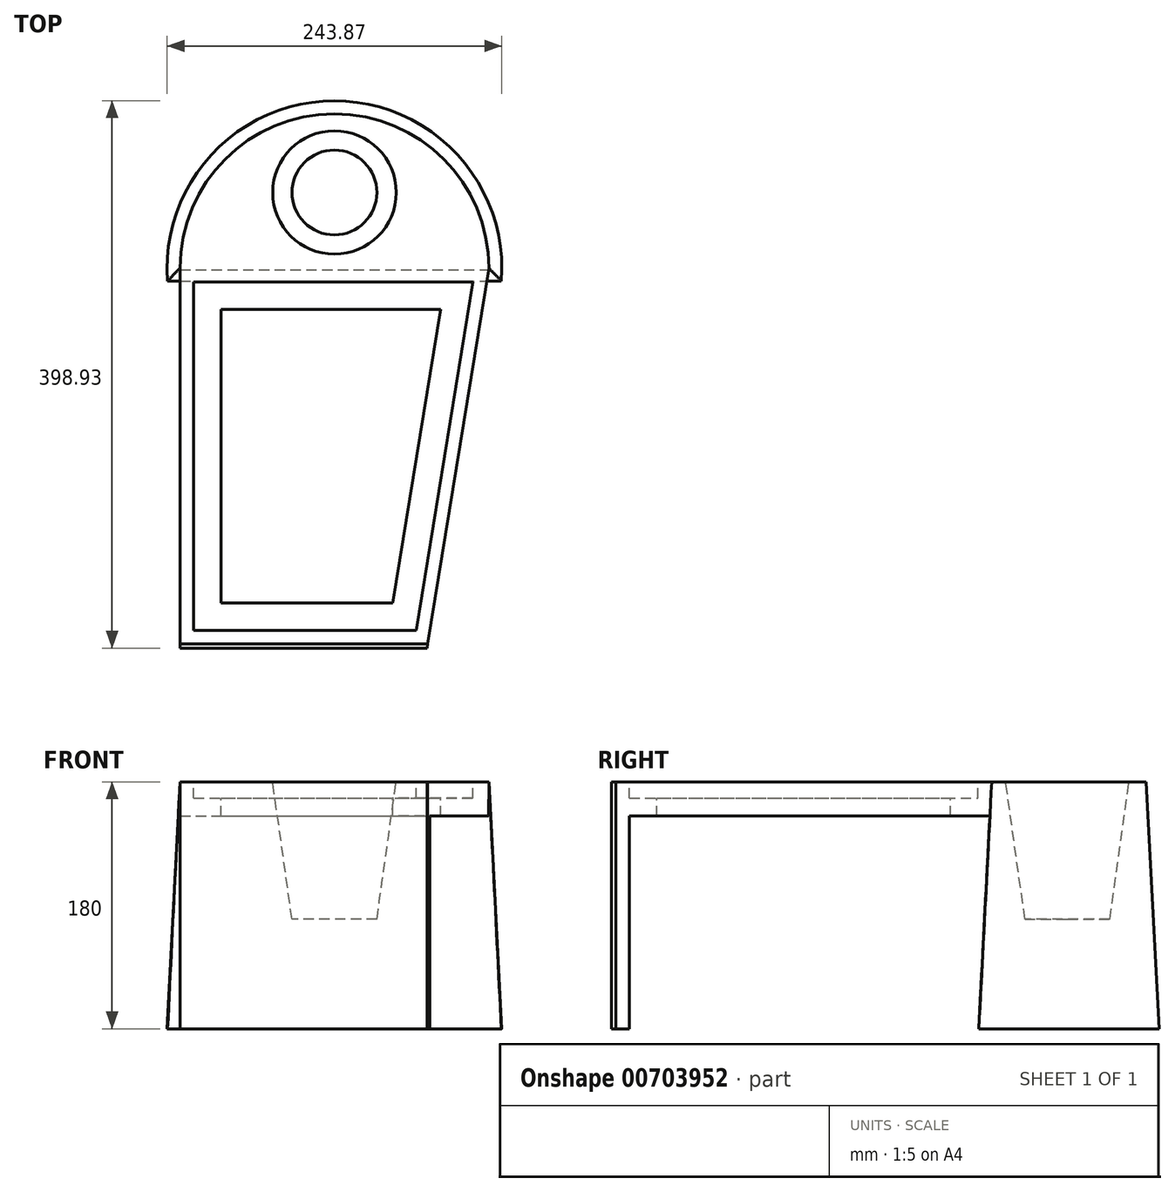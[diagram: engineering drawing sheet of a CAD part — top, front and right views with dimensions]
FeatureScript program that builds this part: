
annotation { "Feature Type Name" : "Feature", "Feature Type Description" : "" }
export const myFeature = defineFeature(function(context is Context, id is Id, definition is map)
    precondition{}
    {
        {
            var Q0;
            Q0=qCreatedBy(makeId("Top.planeOp"),FACE);
            var sketch = newSketch(context, id + "F0", { "sketchPlane" : qUnion([Q0])});
            skLineSegment(sketch, "E0", {"start": v(-80.13, -2.3) * mm, "end": v(99.87, -2.3) * mm});
            skLineSegment(sketch, "E1", {"start": v(-80.13, -2.3) * mm, "end": v(-80.13, 0.7) * mm});
            skArc(sketch, "E2", {"start": v(144.87, 274.7) * mm, "mid": v(32.37, 387.2) * mm, "end": v(-80.13, 274.7) * mm});
            skLineSegment(sketch, "E3", {"start": v(144.87, 274.7) * mm, "end": v(100.35, 0.7) * mm});
            skLineSegment(sketch, "E4", {"start": v(-80.13, 274.7) * mm, "end": v(144.87, 274.7) * mm});
            skLineSegment(sketch, "E5", {"start": v(-80.13, 0.7) * mm, "end": v(100.35, 0.7) * mm});
            skLineSegment(sketch, "E6", {"start": v(-80.13, 0.7) * mm, "end": v(-80.13, 274.7) * mm});
            skLineSegment(sketch, "E7", {"start": v(100.35, 0.7) * mm, "end": v(99.87, -2.3) * mm});
            skLineSegment(sketch, "E8.0", {"start": v(-70.13, 10.7) * mm, "end": v(-70.13, 264.7) * mm});
            skLineSegment(sketch, "E8.1", {"start": v(-70.13, 10.7) * mm, "end": v(91.85, 10.7) * mm});
            skLineSegment(sketch, "E8.2", {"start": v(133.1, 264.7) * mm, "end": v(91.85, 10.7) * mm});
            skLineSegment(sketch, "E8.3", {"start": v(-70.13, 264.7) * mm, "end": v(133.1, 264.7) * mm});
            skLineSegment(sketch, "E9.0", {"start": v(-50.13, 30.7) * mm, "end": v(-50.13, 244.7) * mm});
            skLineSegment(sketch, "E9.1", {"start": v(-50.13, 30.7) * mm, "end": v(74.83, 30.7) * mm});
            skLineSegment(sketch, "E9.2", {"start": v(109.6, 244.7) * mm, "end": v(74.83, 30.7) * mm});
            skLineSegment(sketch, "E9.3", {"start": v(-50.13, 244.7) * mm, "end": v(109.6, 244.7) * mm});
            skCircle(sketch, "E10", {"center": v(32.37, 329.83) * mm, "radius": 45 * mm});
            skPoint(sketch, "E10.centerSnap0", {"position": v(32.37, 387.2) * mm});
            skLineSegment(sketch, "E11", {"start": v(-70.13, 10.7) * mm, "end": v(-80.13, 10.7) * mm});
            skLineSegment(sketch, "E12", {"start": v(91.85, 10.7) * mm, "end": v(101.98, 10.7) * mm});
            skSolve(sketch);
        }
        {
            var Q0;
            Q0=makeQuery(id+"F0.imprint","IMPRINT",FACE,{"disambiguationData":[TD([[makeQuery(id+"F0.imprint","IMPRINT",EDGE,{"derivedFrom":sQuery(id+"F0.wireOp",EDGE,"E0")}),1.0]])]});
            extrude(context, id + "F1", {"entities" : qUnion([Q0]), "oppositeDirection" : true, "depth" : 180 * mm, "offsetDistance" : 25 * mm});
        }
        {
            var Q0;
            {var subQ1=sQuery(id+"F0.wireOp",EDGE,"E5");Q0=makeQuery(id+"F0.imprint","IMPRINT",FACE,{"disambiguationData":[TD([[makeQuery(id+"F0.imprint","IMPRINT",EDGE,{"derivedFrom":subQ1}),1.0]])]});}
            extrude(context, id + "F2", {"entities" : qUnion([Q0]), "oppositeDirection" : true, "depth" : 180 * mm, "offsetDistance" : 25 * mm});
        }
        {
            var Q0;
            {var subQ0=sQuery(id+"F0.wireOp",EDGE,"E4");Q0=makeQuery(id+"F0.imprint","IMPRINT",FACE,{"disambiguationData":[TD([[makeQuery(id+"F0.imprint","IMPRINT",EDGE,{"derivedFrom":subQ0}),-1.0]])]});}
            extrude(context, id + "F3", {"entities" : qUnion([Q0]), "operationType" : NewBodyOperationType.ADD, "oppositeDirection" : true, "depth" : 25 * mm, "offsetDistance" : 25 * mm});
        }
        {
            var Q0;
            Q0=makeQuery(id+"F0.imprint","IMPRINT",FACE,{"disambiguationData":[TD([[makeQuery(id+"F0.imprint","IMPRINT",EDGE,{"derivedFrom":sQuery(id+"F0.wireOp",EDGE,"E10")}),1.0]])]});
            var Q1;
            Q1=makeQuery(id+"F0.imprint","IMPRINT",FACE,{"disambiguationData":[TD([[makeQuery(id+"F0.imprint","IMPRINT",EDGE,{"derivedFrom":sQuery(id+"F0.wireOp",EDGE,"E2")}),1.0]])]});
            extrude(context, id + "F4", {"entities" : qUnion([Q0, Q1]), "operationType" : NewBodyOperationType.ADD, "oppositeDirection" : true, "depth" : 180 * mm, "offsetDistance" : 25 * mm, "hasDraft" : true, "draftAngle" : 3 * degree});
        }
        {
            var Q0;
            Q0=makeQuery(id+"F0.imprint","IMPRINT",FACE,{"disambiguationData":[TD([[makeQuery(id+"F0.imprint","IMPRINT",EDGE,{"derivedFrom":sQuery(id+"F0.wireOp",EDGE,"E8.0")}),-1.0]])]});
            extrude(context, id + "F5", {"entities" : qUnion([Q0]), "operationType" : NewBodyOperationType.ADD, "oppositeDirection" : true, "depth" : 25 * mm, "offsetDistance" : 25 * mm, "hasSecondDirection" : true, "secondDirectionOppositeDirection" : false, "secondDirectionDepth" : -12 * mm});
        }
        {
            var Q0;
            Q0=makeQuery(id+"F0.imprint","IMPRINT",FACE,{"disambiguationData":[TD([[makeQuery(id+"F0.imprint","IMPRINT",EDGE,{"derivedFrom":sQuery(id+"F0.wireOp",EDGE,"E10")}),1.0]])]});
            extrude(context, id + "F6", {"entities" : qUnion([Q0]), "operationType" : NewBodyOperationType.REMOVE, "oppositeDirection" : true, "depth" : 100 * mm, "offsetDistance" : 25 * mm, "hasDraft" : true, "draftAngle" : 8 * degree, "draftPullDirection" : true});
        }
    });
